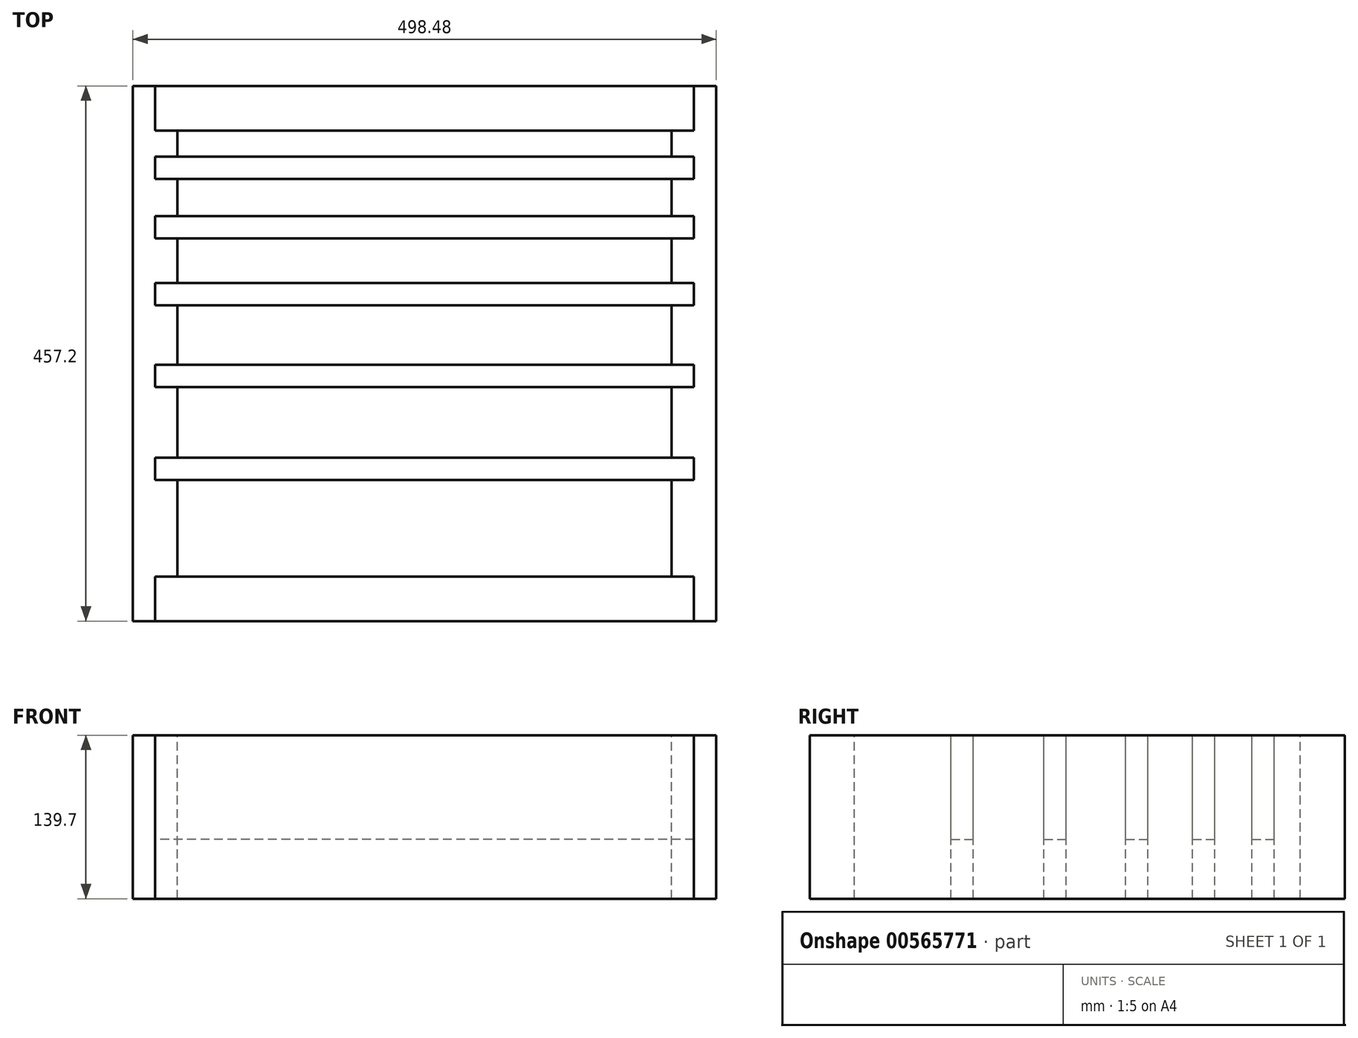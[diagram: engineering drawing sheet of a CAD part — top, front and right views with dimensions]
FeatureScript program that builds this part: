
annotation { "Feature Type Name" : "Feature", "Feature Type Description" : "" }
export const myFeature = defineFeature(function(context is Context, id is Id, definition is map)
    precondition{}
    {
        {
            var Q0;
            Q0=qCreatedBy(makeId("Top.planeOp"),FACE);
            var sketch = newSketch(context, id + "F0", { "sketchPlane" : qUnion([Q0])});
            skLineSegment(sketch, "E0.bottom", {"start": v(-230.19, 0) * mm, "end": v(-249.24, 0) * mm});
            skLineSegment(sketch, "E0.top", {"start": v(-230.19, 457.2) * mm, "end": v(-249.24, 457.2) * mm});
            skLineSegment(sketch, "E0.left", {"start": v(-211.14, 38.1) * mm, "end": v(-211.14, 419.1) * mm});
            skLineSegment(sketch, "E0.right", {"start": v(-249.24, 0) * mm, "end": v(-249.24, 457.2) * mm});
            skLineSegment(sketch, "E1.top", {"start": v(-230.19, 38.1) * mm, "end": v(-211.14, 38.1) * mm});
            skLineSegment(sketch, "E1.left", {"start": v(-230.19, 0) * mm, "end": v(-230.19, 38.1) * mm});
            skPoint(sketch, "E2.orphan", {"position": v(-211.14, 0) * mm});
            skPoint(sketch, "E3.oppositeSnap0", {"position": v(-230.19, 457.2) * mm});
            skLineSegment(sketch, "E3.top", {"start": v(-211.14, 419.1) * mm, "end": v(-230.19, 419.1) * mm});
            skLineSegment(sketch, "E3.right", {"start": v(-230.19, 457.2) * mm, "end": v(-230.19, 419.1) * mm});
            skPoint(sketch, "E4.orphan", {"position": v(-211.14, 457.2) * mm});
            skSolve(sketch);
        }
        {
            var Q0;
            Q0 = qSketchRegion(id + "F0", true);
            extrude(context, id + "F1", {"entities" : qUnion([Q0]), "oppositeDirection" : true, "depth" : 139.7 * mm, "offsetDistance" : 25.4 * mm});
        }
        {
            var Q0;
            Q0=makeQuery(id+"F1.opExtrude","CAP_FACE",FACE,{"disambiguationData":[OSD([sQuery(id+"F0.wireOp",EDGE,"E0.bottom"),sQuery(id+"F0.wireOp",EDGE,"E0.top"),sQuery(id+"F0.wireOp",EDGE,"E0.left"),sQuery(id+"F0.wireOp",EDGE,"E0.right"),sQuery(id+"F0.wireOp",EDGE,"E1.top"),sQuery(id+"F0.wireOp",EDGE,"E1.left"),sQuery(id+"F0.wireOp",EDGE,"E3.top"),sQuery(id+"F0.wireOp",EDGE,"E3.right")])],"isStart":true});
            var sketch = newSketch(context, id + "F2", { "sketchPlane" : qUnion([Q0])});
            skLineSegment(sketch, "E5.bottom", {"start": v(-211.14, 120.65) * mm, "end": v(-230.19, 120.65) * mm});
            skLineSegment(sketch, "E5.top", {"start": v(-211.14, 139.7) * mm, "end": v(-230.19, 139.7) * mm});
            skLineSegment(sketch, "E5.left", {"start": v(-211.14, 120.65) * mm, "end": v(-211.14, 139.7) * mm});
            skLineSegment(sketch, "E5.right", {"start": v(-230.19, 120.65) * mm, "end": v(-230.19, 139.7) * mm});
            skLineSegment(sketch, "E6.bottom", {"start": v(-211.14, 200.03) * mm, "end": v(-230.19, 200.03) * mm});
            skLineSegment(sketch, "E6.top", {"start": v(-211.14, 219.08) * mm, "end": v(-230.19, 219.08) * mm});
            skLineSegment(sketch, "E6.left", {"start": v(-211.14, 200.03) * mm, "end": v(-211.14, 219.08) * mm});
            skLineSegment(sketch, "E6.right", {"start": v(-230.19, 200.03) * mm, "end": v(-230.19, 219.08) * mm});
            skLineSegment(sketch, "E7.bottom", {"start": v(-211.14, 269.88) * mm, "end": v(-230.19, 269.88) * mm});
            skLineSegment(sketch, "E7.top", {"start": v(-211.14, 288.93) * mm, "end": v(-230.19, 288.93) * mm});
            skLineSegment(sketch, "E7.left", {"start": v(-211.14, 269.88) * mm, "end": v(-211.14, 288.93) * mm});
            skLineSegment(sketch, "E7.right", {"start": v(-230.19, 269.88) * mm, "end": v(-230.19, 288.93) * mm});
            skLineSegment(sketch, "E8.bottom", {"start": v(-211.14, 327.03) * mm, "end": v(-230.19, 327.03) * mm});
            skLineSegment(sketch, "E8.top", {"start": v(-211.14, 346.08) * mm, "end": v(-230.19, 346.08) * mm});
            skLineSegment(sketch, "E8.left", {"start": v(-211.14, 327.03) * mm, "end": v(-211.14, 346.08) * mm});
            skLineSegment(sketch, "E8.right", {"start": v(-230.19, 327.03) * mm, "end": v(-230.19, 346.08) * mm});
            skLineSegment(sketch, "E9.bottom", {"start": v(-211.14, 377.83) * mm, "end": v(-230.19, 377.83) * mm});
            skLineSegment(sketch, "E9.top", {"start": v(-211.14, 396.88) * mm, "end": v(-230.19, 396.88) * mm});
            skLineSegment(sketch, "E9.left", {"start": v(-211.14, 377.83) * mm, "end": v(-211.14, 396.88) * mm});
            skLineSegment(sketch, "E9.right", {"start": v(-230.19, 377.83) * mm, "end": v(-230.19, 396.88) * mm});
            skSolve(sketch);
        }
        {
            var Q0;
            Q0 = qSketchRegion(id + "F2", true);
            extrude(context, id + "F3", {"entities" : qUnion([Q0]), "operationType" : NewBodyOperationType.REMOVE, "endBound" : BoundingType.UP_TO_NEXT, "oppositeDirection" : true, "depth" : 25.4 * mm, "offsetDistance" : 25.4 * mm});
        }
        {
            var Q0;
            Q0=makeQuery(id+"F1.opExtrude","SWEPT_BODY",BODY,{"disambiguationData":[OSD([sQuery(id+"F0.wireOp",EDGE,"E0.bottom"),sQuery(id+"F0.wireOp",EDGE,"E0.top"),sQuery(id+"F0.wireOp",EDGE,"E0.left"),sQuery(id+"F0.wireOp",EDGE,"E0.right"),sQuery(id+"F0.wireOp",EDGE,"E1.top"),sQuery(id+"F0.wireOp",EDGE,"E1.left"),sQuery(id+"F0.wireOp",EDGE,"E3.top"),sQuery(id+"F0.wireOp",EDGE,"E3.right")])]});
            var Q1;
            Q1=qCreatedBy(makeId("Right.planeOp"),FACE);
            mirror(context, id + "F4", {"entities" : qUnion([Q0]), "mirrorPlane" : qUnion([Q1])});
        }
        {
            var Q0;
            Q0=makeQuery(id+"F1.opExtrude","CAP_FACE",FACE,{"disambiguationData":[OSD([sQuery(id+"F0.wireOp",EDGE,"E0.bottom"),sQuery(id+"F0.wireOp",EDGE,"E0.top"),sQuery(id+"F0.wireOp",EDGE,"E0.left"),sQuery(id+"F0.wireOp",EDGE,"E0.right"),sQuery(id+"F0.wireOp",EDGE,"E1.top"),sQuery(id+"F0.wireOp",EDGE,"E1.left"),sQuery(id+"F0.wireOp",EDGE,"E3.top"),sQuery(id+"F0.wireOp",EDGE,"E3.right")])],"isStart":true});
            var sketch = newSketch(context, id + "F5", { "sketchPlane" : qUnion([Q0])});
            skPoint(sketch, "E10.oppositeSnap0", {"position": v(-220.66, 38.1) * mm});
            skLineSegment(sketch, "E10.bottom", {"start": v(-230.19, 0) * mm, "end": v(230.19, 0) * mm});
            skLineSegment(sketch, "E10.top", {"start": v(-230.19, 38.1) * mm, "end": v(230.19, 38.1) * mm});
            skLineSegment(sketch, "E10.left", {"start": v(-230.19, 0) * mm, "end": v(-230.19, 38.1) * mm});
            skLineSegment(sketch, "E10.right", {"start": v(230.19, 0) * mm, "end": v(230.19, 38.1) * mm});
            skLineSegment(sketch, "E11.bottom", {"start": v(-230.19, 457.2) * mm, "end": v(230.19, 457.2) * mm});
            skLineSegment(sketch, "E11.top", {"start": v(-230.19, 419.1) * mm, "end": v(230.19, 419.1) * mm});
            skLineSegment(sketch, "E11.left", {"start": v(-230.19, 457.2) * mm, "end": v(-230.19, 419.1) * mm});
            skLineSegment(sketch, "E11.right", {"start": v(230.19, 457.2) * mm, "end": v(230.19, 419.1) * mm});
            skSolve(sketch);
        }
        {
            var Q0;
            Q0 = qSketchRegion(id + "F5", true);
            extrude(context, id + "F6", {"entities" : qUnion([Q0]), "oppositeDirection" : true, "depth" : 139.7 * mm, "offsetDistance" : 25.4 * mm});
        }
        {
            var Q0;
            Q0=makeQuery(id+"F1.opExtrude","CAP_FACE",FACE,{"disambiguationData":[OSD([sQuery(id+"F0.wireOp",EDGE,"E0.bottom"),sQuery(id+"F0.wireOp",EDGE,"E0.top"),sQuery(id+"F0.wireOp",EDGE,"E0.left"),sQuery(id+"F0.wireOp",EDGE,"E0.right"),sQuery(id+"F0.wireOp",EDGE,"E1.top"),sQuery(id+"F0.wireOp",EDGE,"E1.left"),sQuery(id+"F0.wireOp",EDGE,"E3.top"),sQuery(id+"F0.wireOp",EDGE,"E3.right")])],"isStart":true});
            var sketch = newSketch(context, id + "F7", { "sketchPlane" : qUnion([Q0])});
            skLineSegment(sketch, "E12.bottom", {"start": v(-230.19, 120.65) * mm, "end": v(230.19, 120.65) * mm});
            skLineSegment(sketch, "E12.top", {"start": v(-230.19, 139.7) * mm, "end": v(230.19, 139.7) * mm});
            skLineSegment(sketch, "E12.left", {"start": v(-230.19, 120.65) * mm, "end": v(-230.19, 139.7) * mm});
            skLineSegment(sketch, "E12.right", {"start": v(230.19, 120.65) * mm, "end": v(230.19, 139.7) * mm});
            skPoint(sketch, "E13.oppositeSnap0", {"position": v(-220.66, 219.08) * mm});
            skLineSegment(sketch, "E13.bottom", {"start": v(-230.19, 200.03) * mm, "end": v(230.19, 200.03) * mm});
            skLineSegment(sketch, "E13.top", {"start": v(-230.19, 219.08) * mm, "end": v(230.19, 219.08) * mm});
            skLineSegment(sketch, "E13.left", {"start": v(-230.19, 200.03) * mm, "end": v(-230.19, 219.08) * mm});
            skLineSegment(sketch, "E13.right", {"start": v(230.19, 200.03) * mm, "end": v(230.19, 219.08) * mm});
            skPoint(sketch, "E14.oppositeSnap0", {"position": v(-220.66, 288.93) * mm});
            skLineSegment(sketch, "E14.bottom", {"start": v(-230.19, 269.88) * mm, "end": v(230.19, 269.88) * mm});
            skLineSegment(sketch, "E14.top", {"start": v(-230.19, 288.93) * mm, "end": v(230.19, 288.93) * mm});
            skLineSegment(sketch, "E14.left", {"start": v(-230.19, 269.88) * mm, "end": v(-230.19, 288.93) * mm});
            skLineSegment(sketch, "E14.right", {"start": v(230.19, 269.88) * mm, "end": v(230.19, 288.93) * mm});
            skLineSegment(sketch, "E15.bottom", {"start": v(-230.19, 327.03) * mm, "end": v(230.19, 327.03) * mm});
            skLineSegment(sketch, "E15.top", {"start": v(-230.19, 346.08) * mm, "end": v(230.19, 346.08) * mm});
            skLineSegment(sketch, "E15.left", {"start": v(-230.19, 327.03) * mm, "end": v(-230.19, 346.08) * mm});
            skLineSegment(sketch, "E15.right", {"start": v(230.19, 327.03) * mm, "end": v(230.19, 346.08) * mm});
            skLineSegment(sketch, "E16.bottom", {"start": v(-230.19, 377.83) * mm, "end": v(230.19, 377.83) * mm});
            skLineSegment(sketch, "E16.top", {"start": v(-230.19, 396.88) * mm, "end": v(230.19, 396.88) * mm});
            skLineSegment(sketch, "E16.left", {"start": v(-230.19, 377.83) * mm, "end": v(-230.19, 396.88) * mm});
            skLineSegment(sketch, "E16.right", {"start": v(230.19, 377.83) * mm, "end": v(230.19, 396.88) * mm});
            skSolve(sketch);
        }
        {
            var Q0;
            Q0 = qSketchRegion(id + "F7", true);
            extrude(context, id + "F8", {"entities" : qUnion([Q0]), "oppositeDirection" : true, "depth" : 88.9 * mm, "offsetDistance" : 25.4 * mm});
        }
    });
